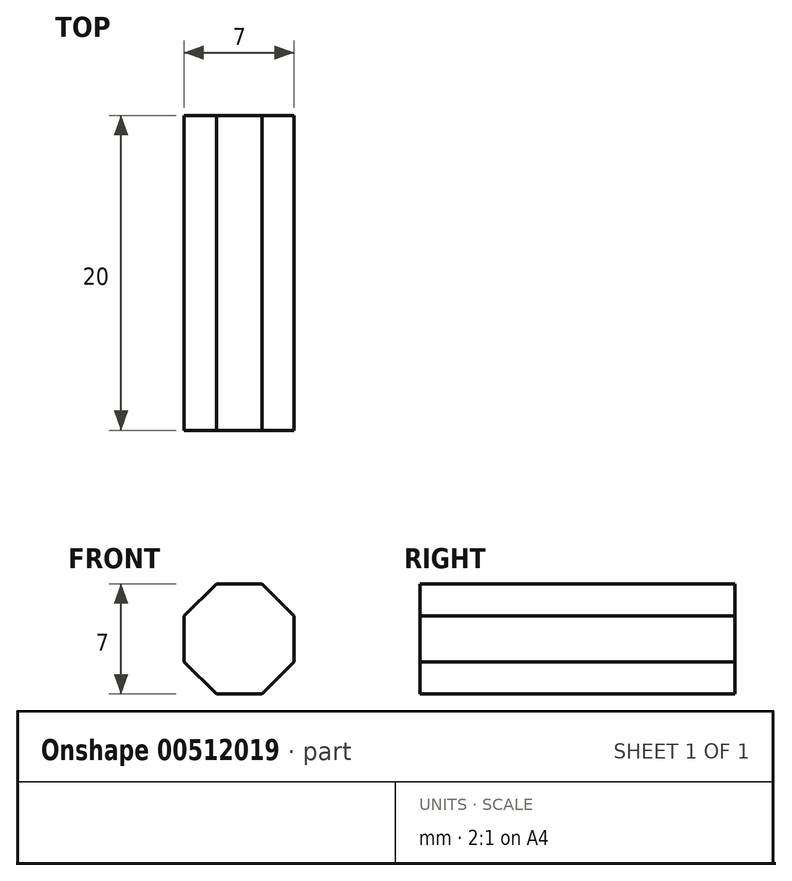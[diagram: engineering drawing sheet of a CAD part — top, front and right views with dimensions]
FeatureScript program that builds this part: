
annotation { "Feature Type Name" : "Feature", "Feature Type Description" : "" }
export const myFeature = defineFeature(function(context is Context, id is Id, definition is map)
    precondition{}
    {
        {
            var Q0;
            Q0=qCreatedBy(makeId("Front.planeOp"),FACE);
            var sketch = newSketch(context, id + "F0", { "sketchPlane" : qUnion([Q0])});
            skCircle(sketch, "E0.cCircle", {"center": v(0, 0) * mm, "radius": 3.5 * mm, "construction": true});
            skLineSegment(sketch, "E0.0", {"start": v(3.5, 1.45) * mm, "end": v(3.5, -1.45) * mm});
            skLineSegment(sketch, "E0.1", {"start": v(3.5, -1.45) * mm, "end": v(1.45, -3.5) * mm});
            skLineSegment(sketch, "E0.2", {"start": v(1.45, -3.5) * mm, "end": v(-1.45, -3.5) * mm});
            skLineSegment(sketch, "E0.3", {"start": v(-1.45, -3.5) * mm, "end": v(-3.5, -1.45) * mm});
            skLineSegment(sketch, "E0.4", {"start": v(-3.5, -1.45) * mm, "end": v(-3.5, 1.45) * mm});
            skLineSegment(sketch, "E0.5", {"start": v(-3.5, 1.45) * mm, "end": v(-1.45, 3.5) * mm});
            skLineSegment(sketch, "E0.6", {"start": v(-1.45, 3.5) * mm, "end": v(1.45, 3.5) * mm});
            skLineSegment(sketch, "E0.7", {"start": v(1.45, 3.5) * mm, "end": v(3.5, 1.45) * mm});
            skPoint(sketch, "E0.0.midPoint", {"position": v(3.5, 0) * mm});
            skSolve(sketch);
        }
        {
            var Q0;
            Q0 = qSketchRegion(id + "F0", true);
            extrude(context, id + "F1", {"entities" : qUnion([Q0]), "depth" : 20 * mm, "offsetDistance" : 25 * mm, "symmetric" : true});
        }
    });
